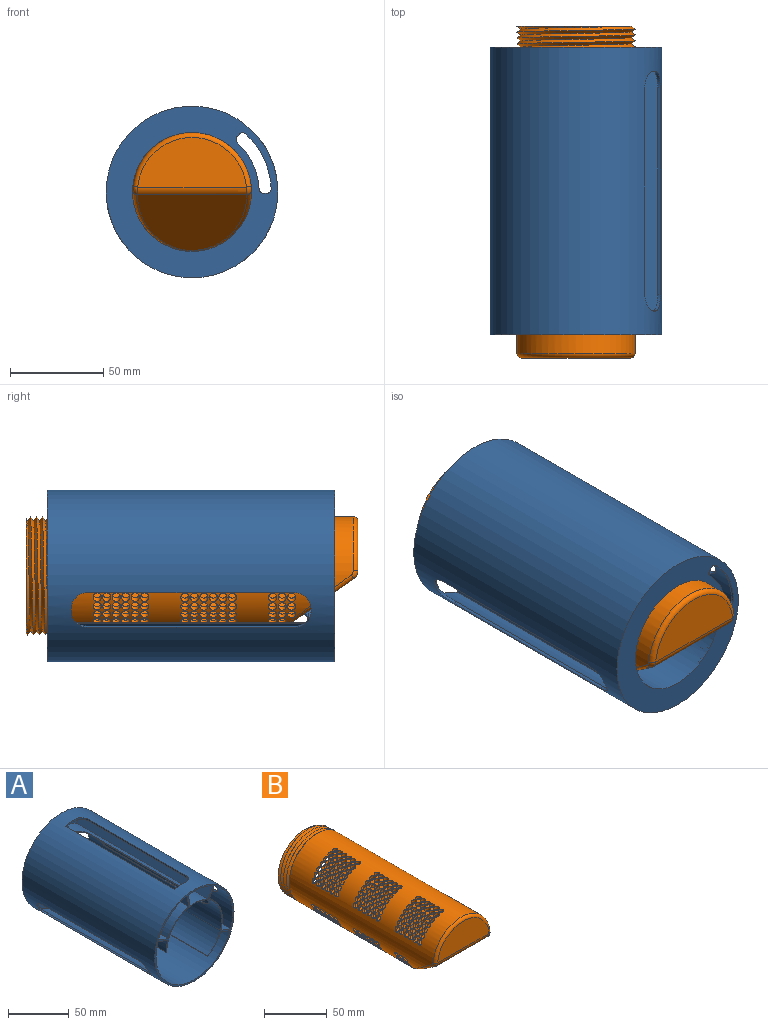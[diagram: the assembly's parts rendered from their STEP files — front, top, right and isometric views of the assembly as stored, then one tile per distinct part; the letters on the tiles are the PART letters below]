
ASSEMBLY  parts=2 mates=1
PART A: 71 faces, bbox 91.9x153.9x91.9 mm
  f0: plane 52.59x27.54mm, normal (0,-1,0), area 397mm2, adj f5,f10,f11,f19,f63,f64,f65,f66
  f1: plane 91.95x91.95mm, normal (0,1,0), area 3221.6mm2, adj f17,f23,f63,f64,f65,f66,f67,f68
  f2: cylinder r=32.51mm len=152.4mm, axis (0,-1,0), area 3515.9mm2, adj f6,f18,f32,f38
  f3: plane 12.7x11.76mm, normal (-0.98,0,-0.17), area 151.6mm2, adj f15,f18,f21,f27
  f4: plane 12.7x11.76mm, normal (0.98,0,0.17), area 151.6mm2, adj f16,f18,f20,f27
  f5: plane 152.4x11.22mm, normal (0.34,0,0.94), area 1819.7mm2, adj f0,f11,f18,f19
  f6: plane 152.4x11.22mm, normal (-0.34,0,-0.94), area 1819.7mm2, adj f2,f12,f18,f32
  f7: plane 12.7x11.76mm, normal (-0.98,0,-0.17), area 151.6mm2, adj f15,f21,f24,f31
  f8: plane 12.7x11.76mm, normal (0.98,0,0.17), area 151.6mm2, adj f16,f20,f24,f30
  f9: plane 152.4x10.34mm, normal (-0.87,0,0.5), area 1819.7mm2, adj f16,f18,f20,f30
  f10: plane 152.4x10.34mm, normal (0.87,0,-0.5), area 1819.7mm2, adj f0,f11,f18,f19
  f11: cylinder r=44.45mm len=152.4mm, axis (0,1,0), area 6660.4mm2, adj f0,f5,f10,f18,f43,f44,f45,f46
  f12: cylinder r=44.45mm len=152.4mm, axis (0,1,0), area 18483.6mm2, adj f6,f13,f18,f32,f47,f48,f49,f50
  f13: plane 152.4x11.22mm, normal (-0.34,0,-0.94), area 1819.7mm2, adj f12,f18,f22,f32
  f14: plane 152.4x11.22mm, normal (0.34,0,0.94), area 1819.7mm2, adj f15,f18,f21,f31
  f15: cylinder r=44.45mm len=152.4mm, axis (0,1,0), area 6641.9mm2, adj f3,f7,f14,f18,f24,f25,f27,f31
  f16: cylinder r=44.45mm len=152.4mm, axis (0,1,0), area 2332.1mm2, adj f4,f8,f9,f18,f24,f27,f28,f30
  f17: cylinder r=45.97mm len=153.92mm, axis (0,1,0), area 36757.5mm2, adj f1,f18,f24,f25,f27,f28,f35,f36
  f18: plane 91.95x91.95mm, normal (0,-1,0), area 592.8mm2, adj f2,f3,f4,f5,f6,f9,f10,f11
  f19: cylinder r=32.51mm len=152.4mm, axis (0,-1,0), area 4100.1mm2, adj f0,f5,f10,f18,f39,f40,f41,f42
  f20: cylinder r=32.51mm len=152.4mm, axis (0,-1,0), area 1316.5mm2, adj f4,f8,f9,f18,f24,f27,f29,f30
  f21: cylinder r=32.51mm len=152.4mm, axis (0,-1,0), area 4461.5mm2, adj f3,f7,f14,f18,f24,f26,f27,f31
  f22: cylinder r=32.51mm len=152.4mm, axis (0,-1,0), area 1786.4mm2, adj f13,f18,f32,f37
  f23: cylinder r=31.88mm len=153.92mm, axis (0,-1,0), area 15805.5mm2, adj f1,f18,f24,f26,f27,f29,f32,f33
  f24: plane 15.76x12.7mm, normal (0,-1,0), area 45.9mm2, adj f7,f8,f15,f16,f17,f20,f21,f23
  f25: plane 127x1.56mm, normal (1,0,0), area 198.6mm2, adj f15,f17,f24,f27
  f26: plane 127x0.67mm, normal (1,0,0), area 85mm2, adj f21,f23,f24,f27
  f27: plane 15.76x12.7mm, normal (0,1,0), area 45.9mm2, adj f3,f4,f15,f16,f17,f20,f21,f23
  f28: plane 111.76x1.56mm, normal (-1,0,0), area 174.8mm2, adj f16,f17,f35,f36
  f29: plane 111.76x0.67mm, normal (-1,0,0), area 74.8mm2, adj f20,f23,f33,f34
  f30: plane 28.53x15.92mm, normal (0,-1,0), area 302.5mm2, adj f8,f9,f16,f20
  f31: plane 35.11x31.8mm, normal (0,-1,0), area 462.9mm2, adj f7,f14,f15,f21
  f32: plane 85.95x58.93mm, normal (0,-1,0), area 1466.4mm2, adj f2,f6,f12,f13,f22,f23,f37,f38
  f33: cylinder r=7.62mm len=7.62mm, axis (0,0,-1), area 7.8mm2, adj f20,f23,f27,f29
  f34: cylinder r=7.62mm len=7.62mm, axis (0,0,1), area 7.8mm2, adj f20,f23,f24,f29
  f35: cylinder r=7.62mm len=7.62mm, axis (0,0,-1), area 18.5mm2, adj f16,f17,f27,f28
  f36: cylinder r=7.62mm len=7.62mm, axis (0,0,1), area 18.5mm2, adj f16,f17,f24,f28
  f37: plane 152.4x0.63mm, normal (0.03,0,-1), area 96.8mm2, adj f18,f22,f23,f32
  f38: plane 152.4x0.56mm, normal (-0.88,0,-0.47), area 96.8mm2, adj f2,f18,f23,f32
  f39: plane 110.74x0.58mm, normal (-0.5,0,0.87), area 74.1mm2, adj f19,f23,f56,f58
  f40: plane 2.52x1.82mm, normal (0,-1,0), area 1.6mm2, adj f19,f23,f54,f56
  f41: plane 110.74x0.58mm, normal (0.5,0,-0.87), area 74.1mm2, adj f19,f23,f52,f54
  f42: plane 2.52x1.82mm, normal (0,1,0), area 1.6mm2, adj f19,f23,f52,f58
  f43: plane 110.74x1.35mm, normal (-0.5,0,0.87), area 173.2mm2, adj f11,f17,f55,f57
  f44: plane 2.96x2.59mm, normal (0,-1,0), area 3.9mm2, adj f11,f17,f53,f55
  f45: plane 110.74x1.35mm, normal (0.5,0,-0.87), area 173.2mm2, adj f11,f17,f51,f53
  f46: plane 2.96x2.59mm, normal (0,1,0), area 3.9mm2, adj f11,f17,f51,f57
  f47: plane 2.96x2.59mm, normal (0,1,0), area 3.9mm2, adj f12,f17,f59,f62
  f48: plane 110.74x1.35mm, normal (0.5,0,-0.87), area 173.2mm2, adj f12,f17,f59,f60
  f49: plane 2.96x2.59mm, normal (0,-1,0), area 3.9mm2, adj f12,f17,f60,f61
  f50: plane 110.74x1.35mm, normal (-0.5,0,0.87), area 173.2mm2, adj f12,f17,f61,f62
  f51: cylinder r=8.89mm len=9.04mm, axis (0.87,0,0.5), area 21.6mm2, adj f11,f17,f45,f46
  f52: cylinder r=8.89mm len=8.89mm, axis (0.87,0,0.5), area 9.1mm2, adj f19,f23,f41,f42
  f53: cylinder r=8.89mm len=9.04mm, axis (-0.87,0,-0.5), area 21.6mm2, adj f11,f17,f44,f45
  f54: cylinder r=8.89mm len=8.89mm, axis (-0.87,0,-0.5), area 9.1mm2, adj f19,f23,f40,f41
  f55: cylinder r=8.89mm len=9.04mm, axis (0.87,0,0.5), area 21.6mm2, adj f11,f17,f43,f44
  f56: cylinder r=8.89mm len=8.89mm, axis (0.87,0,0.5), area 9.1mm2, adj f19,f23,f39,f40
  f57: cylinder r=8.89mm len=9.04mm, axis (-0.87,0,-0.5), area 21.6mm2, adj f11,f17,f43,f46
  f58: cylinder r=8.89mm len=8.89mm, axis (-0.87,0,-0.5), area 9.1mm2, adj f19,f23,f39,f42
  f59: cylinder r=8.89mm len=9.04mm, axis (0.87,0,0.5), area 21.6mm2, adj f12,f17,f47,f48
  f60: cylinder r=8.89mm len=9.04mm, axis (-0.87,0,-0.5), area 21.6mm2, adj f12,f17,f48,f49
  f61: cylinder r=8.89mm len=9.04mm, axis (0.87,0,0.5), area 21.6mm2, adj f12,f17,f49,f50
  f62: cylinder r=8.89mm len=9.04mm, axis (-0.87,0,-0.5), area 21.6mm2, adj f12,f17,f47,f50
  f63: plane 1.52x1.18mm, normal (0.82,0,-0.57), area 2.2mm2, adj f0,f1,f67,f70
  f64: cylinder r=35.9mm len=23.71mm, axis (0,-1,0), area 42.4mm2, adj f0,f1,f67,f68
  f65: plane 1.52x1.44mm, normal (-0.05,0,1), area 2.2mm2, adj f0,f1,f68,f69
  f66: cylinder r=42.42mm len=28.18mm, axis (0,-1,0), area 50.4mm2, adj f0,f1,f69,f70
  f67: cylinder r=2.54mm len=3.44mm, axis (0,-1,0), area 5.8mm2, adj f0,f1,f63,f64
  f68: cylinder r=2.54mm len=2.66mm, axis (0,-1,0), area 5.8mm2, adj f0,f1,f64,f65
  f69: cylinder r=2.54mm len=2.84mm, axis (0,-1,0), area 6.3mm2, adj f0,f1,f65,f66
  f70: cylinder r=2.54mm len=3.67mm, axis (0,-1,0), area 6.3mm2, adj f0,f1,f63,f66
PART B: 215 faces, bbox 70.3x181.8x78.1 mm
  f0: cylinder r=31.75mm len=164.03mm, axis (0,1,0), area 26428.2mm2, adj f4,f12,f13,f14,f15,f16,f17,f18
  f1: cylinder r=29.21mm len=175.26mm, axis (0,1,0), area 26449.6mm2, adj f8,f9,f10,f11,f17,f18,f19,f20
  f2: bspline ~73.05x63.26mm, area 1867.7mm2, adj f3,f4,f8,f12
  f3: bspline ~73.05x63.26mm, area 2117.8mm2, adj f2,f4,f8,f12
  f4: bspline ~76.26x66.04mm, area 29.7mm2, adj f0,f2,f3,f12
  f5: plane 58.42x42.52mm, normal (0,-0.57,-0.82), area 2394.1mm2, adj f6,f16
  f6: cylinder r=5.08mm len=58.41mm, axis (1,0,0), area 284.3mm2, adj f5,f7,f14,f15
  f7: plane 58.18x26.57mm, normal (0,-1,0), area 1186mm2, adj f6,f13
  f8: plane 63.11x63.09mm, normal (0,1,0), area 264.7mm2, adj f1,f2,f3
  f9: plane 58.42x42.52mm, normal (0,0.57,0.82), area 2394.1mm2, adj f1,f10
  f10: cylinder r=2.54mm len=58.41mm, axis (1,0,0), area 142.1mm2, adj f1,f9,f11
  f11: plane 58.18x26.57mm, normal (0,1,0), area 1186mm2, adj f1,f10
  f12: plane 3.26x2.16mm, normal (0.67,0,-0.74), area 4.6mm2, adj f0,f2,f3,f4
  f13: torus R=29.21mm, axis (0,-1,0), area 364.1mm2, adj f0,f7,f14,f15
  f14: bspline ~6.11x4.13mm, area 16.6mm2, adj f0,f6,f13,f16
  f15: bspline ~6.11x4.13mm, area 16.6mm2, adj f0,f6,f13,f16
  f16: bspline ~63.49x43.96mm, area 357.8mm2, adj f0,f5,f14,f15
  f17: cylinder r=2.22mm len=4.45mm, axis (0,0,-1), area 34.1mm2, adj f0,f1,f70
  f18: cylinder r=2.22mm len=4.45mm, axis (0,0,-1), area 36.5mm2, adj f0,f1
  f19: cylinder r=2.22mm len=4.45mm, axis (0,0,-1), area 34.1mm2, adj f0,f1,f69
  f20: cylinder r=2.22mm len=4.45mm, axis (0,0,-1), area 36.5mm2, adj f0,f1
  f21: cylinder r=2.22mm len=4.45mm, axis (0,0,-1), area 34.8mm2, adj f0,f1,f68
  f22: cylinder r=2.22mm len=4.45mm, axis (0,0,-1), area 36.5mm2, adj f0,f1
  f23: cylinder r=2.22mm len=4.45mm, axis (0,0,-1), area 34.8mm2, adj f0,f1,f67
  f24: cylinder r=2.22mm len=4.45mm, axis (0,0,-1), area 36.5mm2, adj f0,f1
  f25: cylinder r=2.22mm len=4.45mm, axis (0,0,-1), area 35.3mm2, adj f0,f1,f66
  f26: cylinder r=2.22mm len=4.45mm, axis (0,0,-1), area 36.5mm2, adj f0,f1
  f27: cylinder r=2.22mm len=4.45mm, axis (0,0,-1), area 34.8mm2, adj f0,f1,f65
  f28: cylinder r=2.22mm len=4.45mm, axis (0,0,-1), area 36.5mm2, adj f0,f1
  f29: cylinder r=2.22mm len=4.45mm, axis (0,0,-1), area 34.1mm2, adj f0,f1,f64
  f30: cylinder r=2.22mm len=4.45mm, axis (0,0,-1), area 36.5mm2, adj f0,f1
  f31: cylinder r=2.22mm len=4.45mm, axis (0,0,-1), area 34.1mm2, adj f0,f1,f63
  f32: cylinder r=2.22mm len=4.45mm, axis (0,0,-1), area 36.5mm2, adj f0,f1
  f33: cylinder r=2.22mm len=4.45mm, axis (0,0,-1), area 34.8mm2, adj f0,f1,f62
  f34: cylinder r=2.22mm len=4.45mm, axis (0,0,-1), area 36.5mm2, adj f0,f1
  f35: cylinder r=2.22mm len=4.45mm, axis (0,0,-1), area 34.1mm2, adj f0,f1,f61
  f36: cylinder r=2.22mm len=4.45mm, axis (0,0,-1), area 36.5mm2, adj f0,f1
  f37: cylinder r=2.22mm len=4.45mm, axis (0,0,-1), area 35.3mm2, adj f0,f1,f60
  f38: cylinder r=2.22mm len=4.45mm, axis (0,0,-1), area 36.5mm2, adj f0,f1
  f39: cylinder r=2.22mm len=4.45mm, axis (0,0,-1), area 34.8mm2, adj f0,f1,f59
  f40: cylinder r=2.22mm len=4.45mm, axis (0,0,-1), area 36.5mm2, adj f0,f1
  f41: cylinder r=2.22mm len=4.45mm, axis (0,0,-1), area 34.8mm2, adj f0,f1,f58
  f42: cylinder r=2.22mm len=4.45mm, axis (0,0,-1), area 36.5mm2, adj f0,f1
  f43: cylinder r=2.22mm len=4.45mm, axis (0,0,-1), area 35.3mm2, adj f0,f1,f57
  f44: cylinder r=2.22mm len=4.45mm, axis (0,0,-1), area 36.5mm2, adj f0,f1
  f45: cylinder r=2.22mm len=4.45mm, axis (0,0,-1), area 35.3mm2, adj f0,f1,f56
  f46: cylinder r=2.22mm len=4.45mm, axis (0,0,-1), area 36.5mm2, adj f0,f1
  f47: cylinder r=2.22mm len=4.45mm, axis (0,0,-1), area 35.3mm2, adj f0,f1,f55
  f48: cylinder r=2.22mm len=4.45mm, axis (0,0,-1), area 36.5mm2, adj f0,f1
  f49: cylinder r=2.22mm len=4.45mm, axis (0,0,-1), area 34.1mm2, adj f0,f1,f54
  f50: cylinder r=2.22mm len=4.45mm, axis (0,0,-1), area 36.5mm2, adj f0,f1
  f51: cylinder r=2.22mm len=4.45mm, axis (0,0,-1), area 35.3mm2, adj f0,f1,f53
  f52: cylinder r=2.22mm len=4.45mm, axis (0,0,-1), area 36.5mm2, adj f0,f1
  f53: cylinder r=2.22mm len=5.86mm, axis (0.71,0,-0.71), area 36.4mm2, adj f0,f1,f51
  f54: cylinder r=2.22mm len=5.83mm, axis (0.71,0,-0.71), area 35.2mm2, adj f0,f1,f49
  f55: cylinder r=2.22mm len=5.86mm, axis (0.71,0,-0.71), area 36.4mm2, adj f0,f1,f47
  f56: cylinder r=2.22mm len=5.86mm, axis (0.71,0,-0.71), area 36.4mm2, adj f0,f1,f45
  f57: cylinder r=2.22mm len=5.86mm, axis (0.71,0,-0.71), area 36.4mm2, adj f0,f1,f43
  f58: cylinder r=2.22mm len=5.84mm, axis (0.71,0,-0.71), area 35.8mm2, adj f0,f1,f41
  f59: cylinder r=2.22mm len=5.84mm, axis (0.71,0,-0.71), area 35.8mm2, adj f0,f1,f39
  f60: cylinder r=2.22mm len=5.86mm, axis (0.71,0,-0.71), area 36.4mm2, adj f0,f1,f37
  f61: cylinder r=2.22mm len=5.83mm, axis (0.71,0,-0.71), area 35.2mm2, adj f0,f1,f35
  f62: cylinder r=2.22mm len=5.84mm, axis (0.71,0,-0.71), area 35.8mm2, adj f0,f1,f33
  f63: cylinder r=2.22mm len=5.83mm, axis (0.71,0,-0.71), area 35.2mm2, adj f0,f1,f31
  f64: cylinder r=2.22mm len=5.83mm, axis (0.71,0,-0.71), area 35.2mm2, adj f0,f1,f29
  f65: cylinder r=2.22mm len=5.84mm, axis (0.71,0,-0.71), area 35.8mm2, adj f0,f1,f27
  f66: cylinder r=2.22mm len=5.86mm, axis (0.71,0,-0.71), area 36.4mm2, adj f0,f1,f25
  f67: cylinder r=2.22mm len=5.84mm, axis (0.71,0,-0.71), area 35.8mm2, adj f0,f1,f23
  f68: cylinder r=2.22mm len=5.84mm, axis (0.71,0,-0.71), area 35.8mm2, adj f0,f1,f21
  f69: cylinder r=2.22mm len=5.83mm, axis (0.71,0,-0.71), area 35.2mm2, adj f0,f1,f19
  f70: cylinder r=2.22mm len=5.83mm, axis (0.71,0,-0.71), area 35.2mm2, adj f0,f1,f17
  f71: cylinder r=2.22mm len=6.36mm, axis (0.71,0,-0.71), area 38.3mm2, adj f0,f1
  f72: cylinder r=2.22mm len=4.94mm, axis (0.71,0,-0.71), area 35.5mm2, adj f0,f1
  f73: cylinder r=2.22mm len=5.01mm, axis (0.71,0,-0.71), area 36.9mm2, adj f0,f1
  f74: cylinder r=2.22mm len=6.34mm, axis (0.71,0,-0.71), area 38.2mm2, adj f0,f1
  f75: cylinder r=2.22mm len=6.36mm, axis (0.71,0,-0.71), area 38.3mm2, adj f0,f1
  f76: cylinder r=2.22mm len=4.95mm, axis (0.71,0,-0.71), area 35.7mm2, adj f0,f1
  f77: cylinder r=2.22mm len=4.94mm, axis (0.71,0,-0.71), area 35.5mm2, adj f0,f1
  f78: cylinder r=2.22mm len=4.95mm, axis (0.71,0,-0.71), area 35.7mm2, adj f0,f1
  f79: cylinder r=2.22mm len=4.94mm, axis (0.71,0,-0.71), area 35.5mm2, adj f0,f1
  f80: cylinder r=2.22mm len=6.36mm, axis (0.71,0,-0.71), area 38.3mm2, adj f0,f1
  f81: cylinder r=2.22mm len=5.01mm, axis (0.71,0,-0.71), area 37mm2, adj f0,f1
  f82: cylinder r=2.22mm len=5.01mm, axis (0.71,0,-0.71), area 36.9mm2, adj f0,f1
  f83: cylinder r=2.22mm len=4.95mm, axis (0.71,0,-0.71), area 35.7mm2, adj f0,f1
  f84: cylinder r=2.22mm len=6.34mm, axis (0.71,0,-0.71), area 38.2mm2, adj f0,f1
  f85: cylinder r=2.22mm len=5.01mm, axis (0.71,0,-0.71), area 37mm2, adj f0,f1
  f86: cylinder r=2.22mm len=6.36mm, axis (0.71,0,-0.71), area 38.3mm2, adj f0,f1
  f87: cylinder r=2.22mm len=4.94mm, axis (0.71,0,-0.71), area 35.5mm2, adj f0,f1
  f88: cylinder r=2.22mm len=4.95mm, axis (0.71,0,-0.71), area 35.7mm2, adj f0,f1
  f89: cylinder r=2.22mm len=4.95mm, axis (0.71,0,-0.71), area 35.7mm2, adj f0,f1
  f90: cylinder r=2.22mm len=5.01mm, axis (0.71,0,-0.71), area 37mm2, adj f0,f1
  f91: cylinder r=2.22mm len=4.94mm, axis (0.71,0,-0.71), area 35.5mm2, adj f0,f1
  f92: cylinder r=2.22mm len=4.95mm, axis (0.71,0,-0.71), area 35.7mm2, adj f0,f1
  f93: cylinder r=2.22mm len=4.94mm, axis (0.71,0,-0.71), area 35.5mm2, adj f0,f1
  f94: cylinder r=2.22mm len=6.36mm, axis (0.71,0,-0.71), area 38.3mm2, adj f0,f1
  f95: cylinder r=2.22mm len=5.01mm, axis (0.71,0,-0.71), area 37mm2, adj f0,f1
  f96: cylinder r=2.22mm len=5.01mm, axis (0.71,0,-0.71), area 37mm2, adj f0,f1
  f97: cylinder r=2.22mm len=4.95mm, axis (0.71,0,-0.71), area 35.7mm2, adj f0,f1
  f98: cylinder r=2.22mm len=6.36mm, axis (0.71,0,-0.71), area 38.3mm2, adj f0,f1
  f99: cylinder r=2.22mm len=6.36mm, axis (0.71,0,-0.71), area 38.3mm2, adj f0,f1
  f100: cylinder r=2.22mm len=4.95mm, axis (0.71,0,-0.71), area 35.7mm2, adj f0,f1
  f101: cylinder r=2.22mm len=4.94mm, axis (0.71,0,-0.71), area 35.5mm2, adj f0,f1
  f102: cylinder r=2.22mm len=4.94mm, axis (0.71,0,-0.71), area 35.5mm2, adj f0,f1
  f103: cylinder r=2.22mm len=5.01mm, axis (0.71,0,-0.71), area 37mm2, adj f0,f1
  f104: cylinder r=2.22mm len=4.95mm, axis (0.71,0,-0.71), area 35.7mm2, adj f0,f1
  f105: cylinder r=2.22mm len=4.94mm, axis (0.71,0,-0.71), area 35.5mm2, adj f0,f1
  f106: cylinder r=2.22mm len=5.01mm, axis (0.71,0,-0.71), area 37mm2, adj f0,f1
  f107: cylinder r=2.22mm len=4.95mm, axis (0.71,0,-0.71), area 35.7mm2, adj f0,f1
  f108: cylinder r=2.22mm len=4.95mm, axis (0.71,0,-0.71), area 35.7mm2, adj f0,f1
  f109: cylinder r=2.22mm len=4.94mm, axis (0.71,0,-0.71), area 35.5mm2, adj f0,f1
  f110: cylinder r=2.22mm len=6.36mm, axis (0.71,0,-0.71), area 38.3mm2, adj f0,f1
  f111: cylinder r=2.22mm len=5.01mm, axis (0.71,0,-0.71), area 37mm2, adj f0,f1
  f112: cylinder r=2.22mm len=6.36mm, axis (0.71,0,-0.71), area 38.3mm2, adj f0,f1
  f113: cylinder r=2.22mm len=5.01mm, axis (0.71,0,-0.71), area 37mm2, adj f0,f1
  f114: cylinder r=2.22mm len=4.94mm, axis (0.71,0,-0.71), area 35.5mm2, adj f0,f1
  f115: cylinder r=2.22mm len=6.36mm, axis (0.71,0,-0.71), area 38.3mm2, adj f0,f1
  f116: cylinder r=2.22mm len=4.95mm, axis (0.71,0,-0.71), area 35.7mm2, adj f0,f1
  f117: cylinder r=2.22mm len=5.01mm, axis (0.71,0,-0.71), area 37mm2, adj f0,f1
  f118: cylinder r=2.22mm len=6.34mm, axis (0.71,0,-0.71), area 38.2mm2, adj f0,f1
  f119: cylinder r=2.22mm len=5.01mm, axis (0.71,0,-0.71), area 36.9mm2, adj f0,f1
  f120: cylinder r=2.22mm len=4.94mm, axis (0.71,0,-0.71), area 35.5mm2, adj f0,f1
  f121: cylinder r=2.22mm len=6.34mm, axis (0.71,0,-0.71), area 38.2mm2, adj f0,f1
  f122: cylinder r=2.22mm len=4.95mm, axis (0.71,0,-0.71), area 35.7mm2, adj f0,f1
  f123: cylinder r=2.22mm len=5.01mm, axis (0.71,0,-0.71), area 36.9mm2, adj f0,f1
  f124: cylinder r=2.22mm len=4.95mm, axis (0.71,0,-0.71), area 35.7mm2, adj f0,f1
  f125: cylinder r=2.22mm len=5.01mm, axis (0.71,0,-0.71), area 37mm2, adj f0,f1
  f126: cylinder r=2.22mm len=4.94mm, axis (0.71,0,-0.71), area 35.5mm2, adj f0,f1
  f127: cylinder r=2.22mm len=4.94mm, axis (0.71,0,-0.71), area 35.5mm2, adj f0,f1
  f128: cylinder r=2.22mm len=4.95mm, axis (0.71,0,-0.71), area 35.7mm2, adj f0,f1
  f129: cylinder r=2.22mm len=6.36mm, axis (0.71,0,-0.71), area 38.3mm2, adj f0,f1
  f130: cylinder r=2.22mm len=4.94mm, axis (0.71,0,-0.71), area 35.5mm2, adj f0,f1
  f131: cylinder r=2.22mm len=4.95mm, axis (0.71,0,-0.71), area 35.7mm2, adj f0,f1
  f132: cylinder r=2.22mm len=6.34mm, axis (0.71,0,-0.71), area 38.2mm2, adj f0,f1
  f133: cylinder r=2.22mm len=6.36mm, axis (0.71,0,-0.71), area 38.3mm2, adj f0,f1
  f134: cylinder r=2.22mm len=5.01mm, axis (0.71,0,-0.71), area 37mm2, adj f0,f1
  f135: cylinder r=2.22mm len=4.94mm, axis (0.71,0,-0.71), area 35.5mm2, adj f0,f1
  f136: cylinder r=2.22mm len=4.94mm, axis (0.71,0,-0.71), area 35.5mm2, adj f0,f1
  f137: cylinder r=2.22mm len=5.01mm, axis (0.71,0,-0.71), area 36.9mm2, adj f0,f1
  f138: cylinder r=2.22mm len=4.95mm, axis (0.71,0,-0.71), area 35.7mm2, adj f0,f1
  f139: cylinder r=2.22mm len=4.95mm, axis (0.71,0,-0.71), area 35.7mm2, adj f0,f1
  f140: cylinder r=2.22mm len=4.94mm, axis (0.71,0,-0.71), area 35.5mm2, adj f0,f1
  f141: cylinder r=2.22mm len=6.34mm, axis (0.71,0,-0.71), area 38.2mm2, adj f0,f1
  f142: cylinder r=2.22mm len=5.01mm, axis (0.71,0,-0.71), area 36.9mm2, adj f0,f1
  f143: cylinder r=2.22mm len=4.94mm, axis (0.71,0,0.71), area 35.5mm2, adj f0,f1
  f144: cylinder r=2.22mm len=6.58mm, axis (0.71,0,0.71), area 39.1mm2, adj f0,f1
  f145: cylinder r=2.22mm len=4.97mm, axis (0.71,0,0.71), area 36mm2, adj f0,f1
  f146: cylinder r=2.22mm len=4.96mm, axis (0.71,0,0.71), area 35.9mm2, adj f0,f1
  f147: cylinder r=2.22mm len=5.04mm, axis (0.71,0,0.71), area 37.5mm2, adj f0,f1
  f148: cylinder r=2.22mm len=6.58mm, axis (0.71,0,0.71), area 39.1mm2, adj f0,f1
  f149: cylinder r=2.22mm len=4.94mm, axis (0.71,0,0.71), area 35.5mm2, adj f0,f1
  f150: cylinder r=2.22mm len=4.97mm, axis (0.71,0,0.71), area 36mm2, adj f0,f1
  f151: cylinder r=2.22mm len=5.04mm, axis (0.71,0,0.71), area 37.4mm2, adj f0,f1
  f152: cylinder r=2.22mm len=4.96mm, axis (0.71,0,0.71), area 35.9mm2, adj f0,f1
  f153: cylinder r=2.22mm len=4.97mm, axis (0.71,0,0.71), area 36mm2, adj f0,f1
  f154: cylinder r=2.22mm len=6.58mm, axis (0.71,0,0.71), area 39.1mm2, adj f0,f1
  f155: cylinder r=2.22mm len=6.58mm, axis (0.71,0,0.71), area 39.1mm2, adj f0,f1
  f156: cylinder r=2.22mm len=5.04mm, axis (0.71,0,0.71), area 37.5mm2, adj f0,f1
  f157: cylinder r=2.22mm len=4.94mm, axis (0.71,0,0.71), area 35.5mm2, adj f0,f1
  f158: cylinder r=2.22mm len=4.96mm, axis (0.71,0,0.71), area 35.9mm2, adj f0,f1
  f159: cylinder r=2.22mm len=4.94mm, axis (0.71,0,0.71), area 35.5mm2, adj f0,f1
  f160: cylinder r=2.22mm len=4.96mm, axis (0.71,0,0.71), area 35.9mm2, adj f0,f1
  f161: cylinder r=2.22mm len=6.61mm, axis (0.71,0,0.71), area 39.3mm2, adj f0,f1
  f162: cylinder r=2.22mm len=4.97mm, axis (0.71,0,0.71), area 36.1mm2, adj f0,f1
  f163: cylinder r=2.22mm len=4.97mm, axis (0.71,0,0.71), area 36.1mm2, adj f0,f1
  f164: cylinder r=2.22mm len=4.94mm, axis (0.71,0,0.71), area 35.5mm2, adj f0,f1
  f165: cylinder r=2.22mm len=6.61mm, axis (0.71,0,0.71), area 39.3mm2, adj f0,f1
  f166: cylinder r=2.22mm len=5.04mm, axis (0.71,0,0.71), area 37.4mm2, adj f0,f1
  f167: cylinder r=2.22mm len=4.97mm, axis (0.71,0,0.71), area 36mm2, adj f0,f1
  f168: cylinder r=2.22mm len=4.94mm, axis (0.71,0,0.71), area 35.5mm2, adj f0,f1
  f169: cylinder r=2.22mm len=6.58mm, axis (0.71,0,0.71), area 39.1mm2, adj f0,f1
  f170: cylinder r=2.22mm len=5.04mm, axis (0.71,0,0.71), area 37.5mm2, adj f0,f1
  f171: cylinder r=2.22mm len=5.04mm, axis (0.71,0,0.71), area 37.5mm2, adj f0,f1
  f172: cylinder r=2.22mm len=4.96mm, axis (0.71,0,0.71), area 35.9mm2, adj f0,f1
  f173: cylinder r=2.22mm len=4.97mm, axis (0.71,0,0.71), area 36mm2, adj f0,f1
  f174: cylinder r=2.22mm len=6.58mm, axis (0.71,0,0.71), area 39.1mm2, adj f0,f1
  f175: cylinder r=2.22mm len=4.97mm, axis (0.71,0,0.71), area 36mm2, adj f0,f1
  f176: cylinder r=2.22mm len=6.58mm, axis (0.71,0,0.71), area 39.1mm2, adj f0,f1
  f177: cylinder r=2.22mm len=4.96mm, axis (0.71,0,0.71), area 35.9mm2, adj f0,f1
  f178: cylinder r=2.22mm len=4.94mm, axis (0.71,0,0.71), area 35.5mm2, adj f0,f1
  f179: cylinder r=2.22mm len=4.94mm, axis (0.71,0,0.71), area 35.5mm2, adj f0,f1
  f180: cylinder r=2.22mm len=4.97mm, axis (0.71,0,0.71), area 36mm2, adj f0,f1
  f181: cylinder r=2.22mm len=5.04mm, axis (0.71,0,0.71), area 37.5mm2, adj f0,f1
  f182: cylinder r=2.22mm len=4.96mm, axis (0.71,0,0.71), area 35.9mm2, adj f0,f1
  f183: cylinder r=2.22mm len=4.94mm, axis (0.71,0,0.71), area 35.5mm2, adj f0,f1
  f184: cylinder r=2.22mm len=4.96mm, axis (0.71,0,0.71), area 35.9mm2, adj f0,f1
  f185: cylinder r=2.22mm len=6.61mm, axis (0.71,0,0.71), area 39.3mm2, adj f0,f1
  f186: cylinder r=2.22mm len=4.97mm, axis (0.71,0,0.71), area 36.1mm2, adj f0,f1
  f187: cylinder r=2.22mm len=4.97mm, axis (0.71,0,0.71), area 36mm2, adj f0,f1
  f188: cylinder r=2.22mm len=4.94mm, axis (0.71,0,0.71), area 35.5mm2, adj f0,f1
  f189: cylinder r=2.22mm len=6.58mm, axis (0.71,0,0.71), area 39.1mm2, adj f0,f1
  f190: cylinder r=2.22mm len=5.04mm, axis (0.71,0,0.71), area 37.4mm2, adj f0,f1
  f191: cylinder r=2.22mm len=6.61mm, axis (0.71,0,0.71), area 39.3mm2, adj f0,f1
  f192: cylinder r=2.22mm len=5.04mm, axis (0.71,0,0.71), area 37.5mm2, adj f0,f1
  f193: cylinder r=2.22mm len=4.94mm, axis (0.71,0,0.71), area 35.5mm2, adj f0,f1
  f194: cylinder r=2.22mm len=4.96mm, axis (0.71,0,0.71), area 35.9mm2, adj f0,f1
  f195: cylinder r=2.22mm len=4.96mm, axis (0.71,0,0.71), area 35.9mm2, adj f0,f1
  f196: cylinder r=2.22mm len=5.04mm, axis (0.71,0,0.71), area 37.4mm2, adj f0,f1
  f197: cylinder r=2.22mm len=4.97mm, axis (0.71,0,0.71), area 36.1mm2, adj f0,f1
  f198: cylinder r=2.22mm len=4.94mm, axis (0.71,0,0.71), area 35.5mm2, adj f0,f1
  f199: cylinder r=2.22mm len=6.61mm, axis (0.71,0,0.71), area 39.3mm2, adj f0,f1
  f200: cylinder r=2.22mm len=5.04mm, axis (0.71,0,0.71), area 37.4mm2, adj f0,f1
  f201: cylinder r=2.22mm len=4.94mm, axis (0.71,0,0.71), area 35.5mm2, adj f0,f1
  f202: cylinder r=2.22mm len=4.96mm, axis (0.71,0,0.71), area 35.9mm2, adj f0,f1
  f203: cylinder r=2.22mm len=4.96mm, axis (0.71,0,0.71), area 35.9mm2, adj f0,f1
  f204: cylinder r=2.22mm len=5.04mm, axis (0.71,0,0.71), area 37.4mm2, adj f0,f1
  f205: cylinder r=2.22mm len=4.97mm, axis (0.71,0,0.71), area 36.1mm2, adj f0,f1
  f206: cylinder r=2.22mm len=4.94mm, axis (0.71,0,0.71), area 35.5mm2, adj f0,f1
  f207: cylinder r=2.22mm len=5.04mm, axis (0.71,0,0.71), area 37.5mm2, adj f0,f1
  f208: cylinder r=2.22mm len=4.96mm, axis (0.71,0,0.71), area 35.9mm2, adj f0,f1
  f209: cylinder r=2.22mm len=4.97mm, axis (0.71,0,0.71), area 36mm2, adj f0,f1
  f210: cylinder r=2.22mm len=6.58mm, axis (0.71,0,0.71), area 39.1mm2, adj f0,f1
  f211: cylinder r=2.22mm len=4.96mm, axis (0.71,0,0.71), area 35.9mm2, adj f0,f1
  f212: cylinder r=2.22mm len=4.94mm, axis (0.71,0,0.71), area 35.5mm2, adj f0,f1
  f213: cylinder r=2.22mm len=4.97mm, axis (0.71,0,0.71), area 36.1mm2, adj f0,f1
  f214: cylinder r=2.22mm len=6.61mm, axis (0.71,0,0.71), area 39.3mm2, adj f0,f1
PLACE A rot(axis=(-0.89,0,-0.45),180deg) t=(0,-11.43,0)mm
PLACE B at identity fixed
MATE revolute A.f12 <-> B.f0  axis (0,-1,0) through (0,-11.43,0)mm
